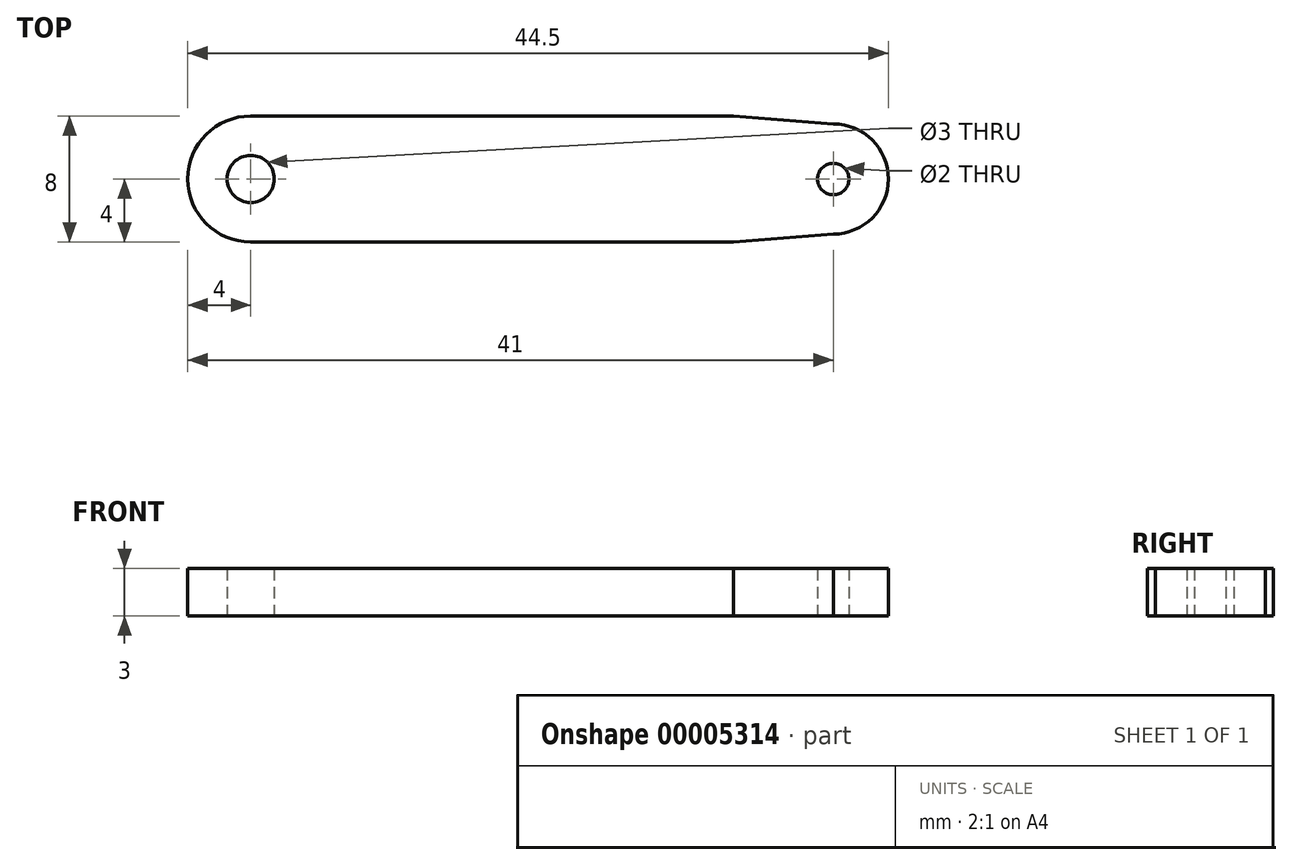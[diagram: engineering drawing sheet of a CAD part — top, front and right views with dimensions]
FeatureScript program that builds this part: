
annotation { "Feature Type Name" : "Feature", "Feature Type Description" : "" }
export const myFeature = defineFeature(function(context is Context, id is Id, definition is map)
    precondition{}
    {
        {
            var Q0;
            Q0=qCreatedBy(makeId("Top.planeOp"),FACE);
            var sketch = newSketch(context, id + "F0", { "sketchPlane" : qUnion([Q0])});
            skCircle(sketch, "E0", {"center": v(0, 0) * mm, "radius": 1.5 * mm});
            skCircle(sketch, "E1", {"center": v(0, 0) * mm, "radius": 4 * mm});
            skCircle(sketch, "E2", {"center": v(37, 0) * mm, "radius": 1 * mm});
            skCircle(sketch, "E3", {"center": v(37, 0) * mm, "radius": 3.5 * mm});
            skLineSegment(sketch, "E4", {"start": v(0, 4) * mm, "end": v(30.65, 4) * mm});
            skLineSegment(sketch, "E5", {"start": v(0, -4) * mm, "end": v(30.65, -4) * mm});
            skLineSegment(sketch, "E6", {"start": v(37, -3.5) * mm, "end": v(37, 3.5) * mm});
            skLineSegment(sketch, "E7", {"start": v(30.65, 4) * mm, "end": v(30.65, -4) * mm});
            skLineSegment(sketch, "E8", {"start": v(37, 3.5) * mm, "end": v(30.65, 4) * mm});
            skLineSegment(sketch, "E9", {"start": v(37, -3.5) * mm, "end": v(30.65, -4) * mm});
            skLineSegment(sketch, "E10.trimOffspring", {"start": v(37, 4) * mm, "end": v(37.23, 4) * mm});
            skPoint(sketch, "E11.orphan", {"position": v(37, -11.3) * mm});
            skSolve(sketch);
        }
        {
            var Q0;
            Q0=makeQuery(id+"F0.imprint","IMPRINT",FACE,{"disambiguationData":[TD([[makeQuery(id+"F0.imprint","IMPRINT",EDGE,{"derivedFrom":sQuery(id+"F0.wireOp",EDGE,"E0")}),-1.0]])]});
            var Q1;
            {var subQ1=sQuery(id+"F0.wireOp",EDGE,"E4");Q1=makeQuery(id+"F0.imprint","IMPRINT",FACE,{"disambiguationData":[TD([[makeQuery(id+"F0.imprint","IMPRINT",EDGE,{"derivedFrom":subQ1}),-1.0]])]});}
            var Q2;
            Q2=makeQuery(id+"F0.imprint","IMPRINT",FACE,{"disambiguationData":[TD([[makeQuery(id+"F0.imprint","IMPRINT",EDGE,{"derivedFrom":sQuery(id+"F0.wireOp",EDGE,"E7")}),1.0]])]});
            var Q3;
            {var subQ0=sQuery(id+"F0.wireOp",EDGE,"E6");var subQ1=sQuery(id+"F0.wireOp",EDGE,"E2");var subQ5=makeQuery(id+"F0.imprint","INTERSECT",VERTEX,{"disambiguationData":[OD(0.0)],"derivedFrom":[subQ1,subQ0]});Q3=makeQuery(id+"F0.imprint","IMPRINT",FACE,{"disambiguationData":[TD([[makeQuery(id+"F0.imprint","IMPRINT",EDGE,{"disambiguationData":[TD([[subQ5,1.0]])],"derivedFrom":subQ1}),-1.0]])]});}
            var Q4;
            {var subQ0=sQuery(id+"F0.wireOp",EDGE,"E6");var subQ1=sQuery(id+"F0.wireOp",EDGE,"E2");var subQ5=makeQuery(id+"F0.imprint","INTERSECT",VERTEX,{"disambiguationData":[OD(0.0)],"derivedFrom":[subQ1,subQ0]});Q4=makeQuery(id+"F0.imprint","IMPRINT",FACE,{"disambiguationData":[TD([[makeQuery(id+"F0.imprint","IMPRINT",EDGE,{"disambiguationData":[TD([[subQ5,-1.0]])],"derivedFrom":subQ1}),-1.0]])]});}
            extrude(context, id + "F1", {"entities" : qUnion([Q0, Q1, Q2, Q3, Q4]), "depth" : 3 * mm});
        }
    });
